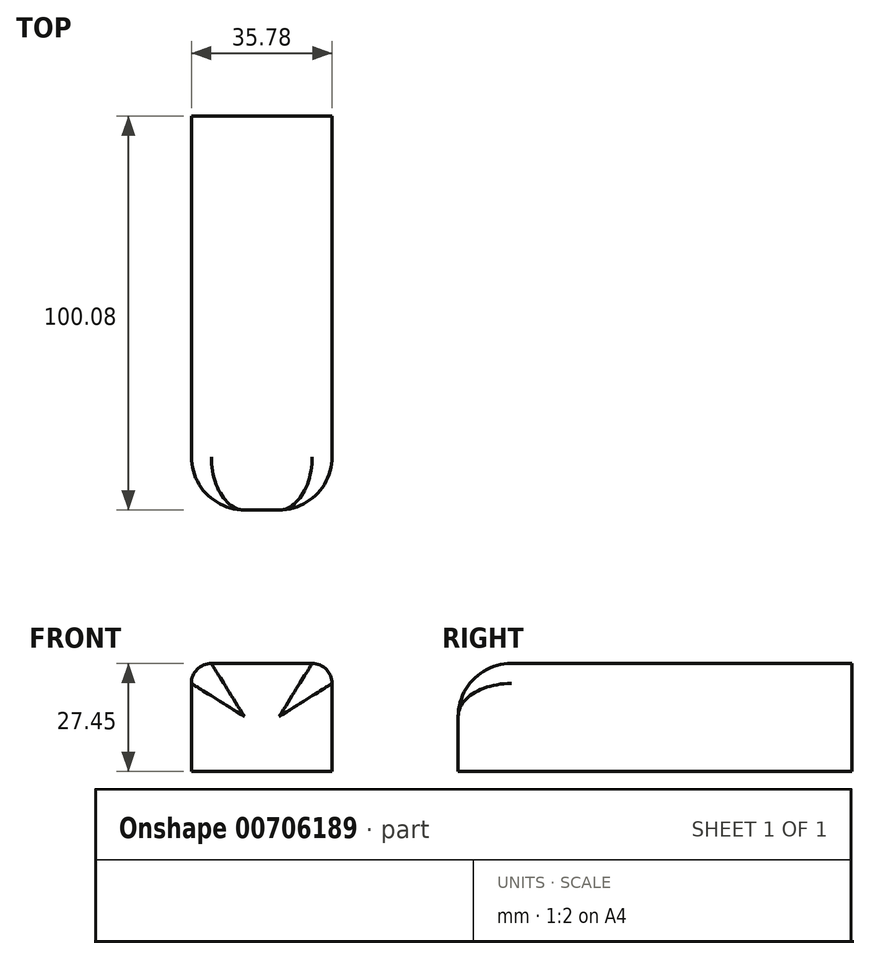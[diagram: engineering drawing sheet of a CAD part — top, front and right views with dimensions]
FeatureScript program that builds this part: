
annotation { "Feature Type Name" : "Feature", "Feature Type Description" : "" }
export const myFeature = defineFeature(function(context is Context, id is Id, definition is map)
    precondition{}
    {
        {
            var Q0;
            Q0=qCreatedBy(makeId("Front.planeOp"),FACE);
            var sketch = newSketch(context, id + "F0", { "sketchPlane" : qUnion([Q0])});
            skLineSegment(sketch, "E0.bottom", {"start": v(0, 0) * mm, "end": v(35.78, 0) * mm});
            skLineSegment(sketch, "E0.top", {"start": v(0, 27.45) * mm, "end": v(35.78, 27.45) * mm});
            skLineSegment(sketch, "E0.left", {"start": v(0, 0) * mm, "end": v(0, 27.45) * mm});
            skLineSegment(sketch, "E0.right", {"start": v(35.78, 0) * mm, "end": v(35.78, 27.45) * mm});
            skSolve(sketch);
        }
        {
            var Q0;
            Q0=makeQuery(id+"F0.imprint","IMPRINT",FACE,{"disambiguationData":[TD([[makeQuery(id+"F0.imprint","IMPRINT",EDGE,{"derivedFrom":sQuery(id+"F0.wireOp",EDGE,"E0.bottom")}),1.0]])]});
            extrude(context, id + "F1", {"entities" : qUnion([Q0]), "depth" : 100.08 * mm, "offsetDistance" : 25.4 * mm});
        }
        {
            var Q0;
            Q0=makeQuery(id+"F1.opExtrude","SWEPT_EDGE",EDGE,{"disambiguationData":[OSD([sQuery(id+"F0.wireOp",EDGE,"E0.top"),sQuery(id+"F0.wireOp",EDGE,"E0.right")])]});
            var Q1;
            Q1=makeQuery(id+"F1.opExtrude","SWEPT_EDGE",EDGE,{"disambiguationData":[OSD([sQuery(id+"F0.wireOp",EDGE,"E0.top"),sQuery(id+"F0.wireOp",EDGE,"E0.left")])]});
            fillet(context, id + "F2", {"entities" : qUnion([Q0, Q1]), "radius" : 5.08 * mm, "tangentPropagation" : true, "allowEdgeOverflow" : false});
        }
        {
            var Q0;
            Q0=makeQuery(id+"F1.opExtrude","CAP_EDGE",EDGE,{"disambiguationData":[OSD([sQuery(id+"F0.wireOp",EDGE,"E0.top")])],"isStart":false});
            fillet(context, id + "F3", {"entities" : qUnion([Q0]), "radius" : 13.5 * mm, "tangentPropagation" : true, "allowEdgeOverflow" : false});
        }
    });
